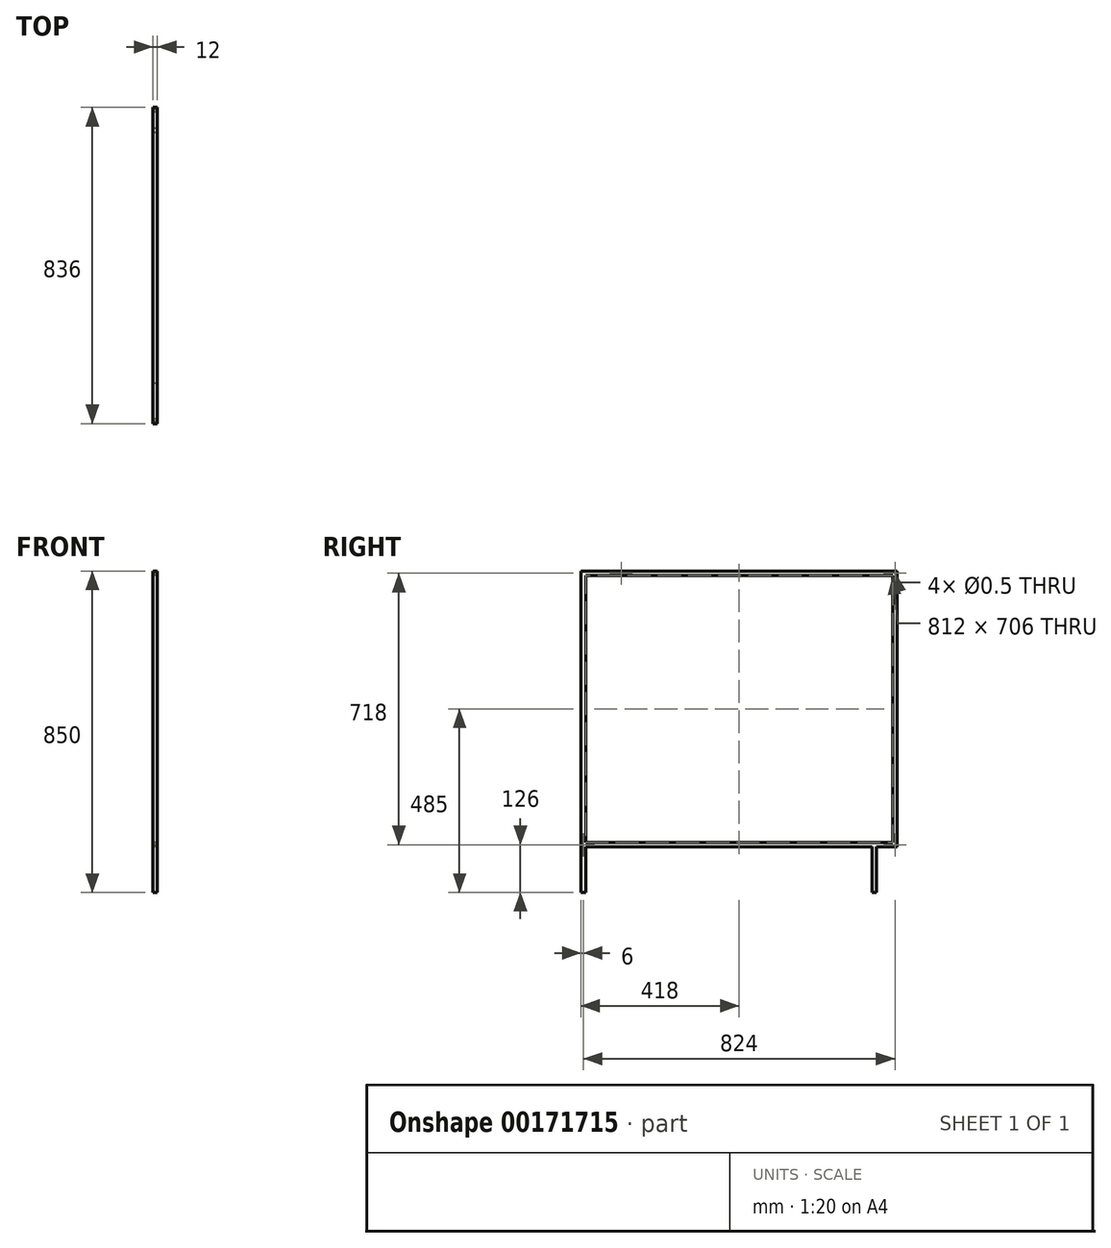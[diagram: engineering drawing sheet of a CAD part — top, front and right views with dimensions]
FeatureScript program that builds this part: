
annotation { "Feature Type Name" : "Feature", "Feature Type Description" : "" }
export const myFeature = defineFeature(function(context is Context, id is Id, definition is map)
    precondition{}
    {
        {
            var Q0;
            Q0=qCreatedBy(makeId("Right.planeOp"),FACE);
            var sketch = newSketch(context, id + "F0", { "sketchPlane" : qUnion([Q0])});
            skLineSegment(sketch, "E0.bottom", {"start": v(418, -365) * mm, "end": v(-418, -365) * mm});
            skLineSegment(sketch, "E0.top", {"start": v(418, 365) * mm, "end": v(-418, 365) * mm});
            skLineSegment(sketch, "E0.left", {"start": v(418, -365) * mm, "end": v(418, 365) * mm});
            skLineSegment(sketch, "E0.right", {"start": v(-418, -365) * mm, "end": v(-418, 365) * mm});
            skPoint(sketch, "E0.middle", {"position": v(0, 0) * mm});
            skLineSegment(sketch, "E1.0", {"start": v(406, 353) * mm, "end": v(-406, 353) * mm});
            skLineSegment(sketch, "E1.1", {"start": v(406, -353) * mm, "end": v(406, 353) * mm});
            skLineSegment(sketch, "E1.2", {"start": v(406, -353) * mm, "end": v(-406, -353) * mm});
            skLineSegment(sketch, "E1.3", {"start": v(-406, -353) * mm, "end": v(-406, 353) * mm});
            skLineSegment(sketch, "E2.bottom", {"start": v(-418, -365) * mm, "end": v(-406, -365) * mm});
            skLineSegment(sketch, "E2.top", {"start": v(-418, -485) * mm, "end": v(-406, -485) * mm});
            skLineSegment(sketch, "E2.left", {"start": v(-418, -365) * mm, "end": v(-418, -485) * mm});
            skLineSegment(sketch, "E2.right", {"start": v(-406, -365) * mm, "end": v(-406, -485) * mm});
            skPoint(sketch, "E3", {"position": v(363, -365) * mm});
            skLineSegment(sketch, "E4.bottom", {"start": v(363, -365) * mm, "end": v(351, -365) * mm});
            skLineSegment(sketch, "E4.top", {"start": v(363, -485) * mm, "end": v(351, -485) * mm});
            skLineSegment(sketch, "E4.left", {"start": v(363, -365) * mm, "end": v(363, -485) * mm});
            skLineSegment(sketch, "E4.right", {"start": v(351, -365) * mm, "end": v(351, -485) * mm});
            skLineSegment(sketch, "E5.bottom", {"start": v(-406, -353) * mm, "end": v(-418, -353) * mm});
            skLineSegment(sketch, "E5.top", {"start": v(-406, -365) * mm, "end": v(-418, -365) * mm});
            skLineSegment(sketch, "E5.left", {"start": v(-406, -353) * mm, "end": v(-406, -365) * mm});
            skLineSegment(sketch, "E5.right", {"start": v(-418, -353) * mm, "end": v(-418, -365) * mm});
            skPoint(sketch, "E6", {"position": v(-412, -359) * mm});
            skLineSegment(sketch, "E7.bottom", {"start": v(406, -353) * mm, "end": v(418, -353) * mm});
            skLineSegment(sketch, "E7.top", {"start": v(406, -365) * mm, "end": v(418, -365) * mm});
            skLineSegment(sketch, "E7.left", {"start": v(406, -353) * mm, "end": v(406, -365) * mm});
            skLineSegment(sketch, "E7.right", {"start": v(418, -353) * mm, "end": v(418, -365) * mm});
            skPoint(sketch, "E8", {"position": v(412, -359) * mm});
            skLineSegment(sketch, "E9.bottom", {"start": v(418, 365) * mm, "end": v(406, 365) * mm});
            skLineSegment(sketch, "E9.top", {"start": v(418, 353) * mm, "end": v(406, 353) * mm});
            skLineSegment(sketch, "E9.left", {"start": v(418, 365) * mm, "end": v(418, 353) * mm});
            skLineSegment(sketch, "E9.right", {"start": v(406, 365) * mm, "end": v(406, 353) * mm});
            skPoint(sketch, "E10", {"position": v(412, 359) * mm});
            skLineSegment(sketch, "E11.bottom", {"start": v(-318, 365) * mm, "end": v(-306, 365) * mm});
            skLineSegment(sketch, "E11.top", {"start": v(-318, 353) * mm, "end": v(-306, 353) * mm});
            skLineSegment(sketch, "E11.left", {"start": v(-318, 365) * mm, "end": v(-318, 353) * mm});
            skLineSegment(sketch, "E11.right", {"start": v(-306, 365) * mm, "end": v(-306, 353) * mm});
            skPoint(sketch, "E12", {"position": v(-312, 359) * mm});
            skSolve(sketch);
        }
        {
            var Q0;
            Q0 = qSketchRegion(id + "F0", true);
            extrude(context, id + "F1", {"entities" : qUnion([Q0]), "depth" : 12 * mm});
        }
        {
            var Q0;
            Q0=sQuery(id+"F0.wireOp",VERTEX,"E10");
            var Q1;
            Q1=sQuery(id+"F0.wireOp",VERTEX,"E8");
            var Q2;
            Q2=sQuery(id+"F0.wireOp",VERTEX,"E6");
            var Q3;
            Q3=sQuery(id+"F0.wireOp",VERTEX,"E12");
            var Q4;
            Q4=makeQuery(id+"F1.opExtrude","SWEPT_BODY",BODY,{"disambiguationData":[OSD([sQuery(id+"F0.wireOp",EDGE,"E0.bottom"),sQuery(id+"F0.wireOp",EDGE,"E0.top"),sQuery(id+"F0.wireOp",EDGE,"E0.left"),sQuery(id+"F0.wireOp",EDGE,"E0.right"),sQuery(id+"F0.wireOp",EDGE,"E1.0"),sQuery(id+"F0.wireOp",EDGE,"E1.1"),sQuery(id+"F0.wireOp",EDGE,"E1.2"),sQuery(id+"F0.wireOp",EDGE,"E1.3"),sQuery(id+"F0.wireOp",EDGE,"E2.top"),sQuery(id+"F0.wireOp",EDGE,"E2.left"),sQuery(id+"F0.wireOp",EDGE,"E2.right"),sQuery(id+"F0.wireOp",EDGE,"E4.top"),sQuery(id+"F0.wireOp",EDGE,"E4.left"),sQuery(id+"F0.wireOp",EDGE,"E4.right"),sQuery(id+"F0.wireOp",EDGE,"E5.right"),sQuery(id+"F0.wireOp",EDGE,"E7.top"),sQuery(id+"F0.wireOp",EDGE,"E7.right"),sQuery(id+"F0.wireOp",EDGE,"E9.bottom"),sQuery(id+"F0.wireOp",EDGE,"E9.left"),sQuery(id+"F0.wireOp",EDGE,"E11.bottom"),sQuery(id+"F0.wireOp",EDGE,"E11.top")])]});
            hole(context, id + "F2", {"style" : HoleStyle.C_SINK, "endStyle" : HoleEndStyle.BLIND, "oppositeDirection" : true, "holeDiameter" : 0.5 * mm, "cSinkDiameter" : 0.5 * mm, "cSinkAngle" : 90 * degree, "holeDepth" : 12 * mm, "startFromSketch" : true, "locations" : qUnion([Q0, Q1, Q2, Q3]), "scope" : qUnion([Q4])});
        }
    });
